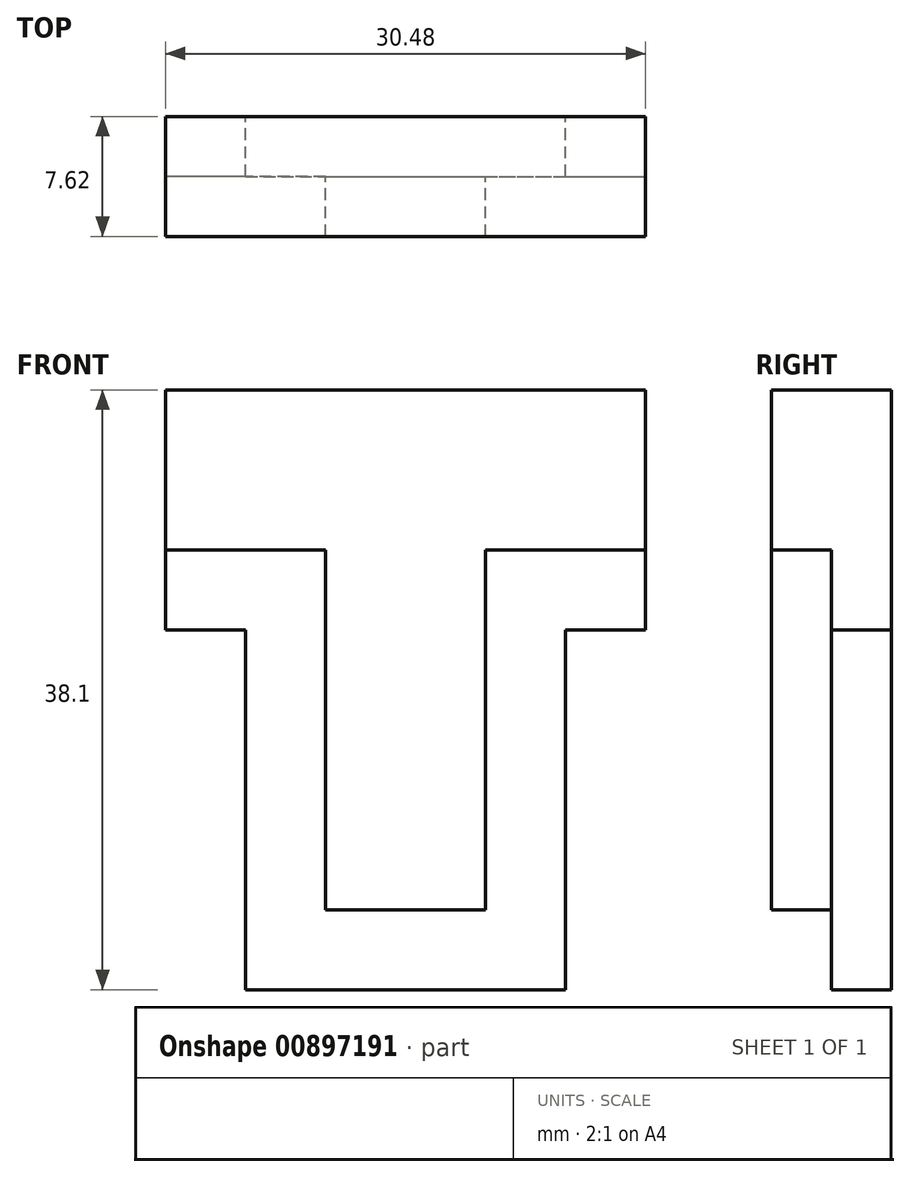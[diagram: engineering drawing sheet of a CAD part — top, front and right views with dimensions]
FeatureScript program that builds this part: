
annotation { "Feature Type Name" : "Feature", "Feature Type Description" : "" }
export const myFeature = defineFeature(function(context is Context, id is Id, definition is map)
    precondition{}
    {
        {
            var Q0;
            Q0=qCreatedBy(makeId("Front.planeOp"),FACE);
            var sketch = newSketch(context, id + "F0", { "sketchPlane" : qUnion([Q0])});
            skLineSegment(sketch, "E0.top", {"start": v(-25.4, -17.78) * mm, "end": v(-5.08, -17.78) * mm});
            skLineSegment(sketch, "E0.left", {"start": v(-25.4, 0) * mm, "end": v(-25.4, -17.78) * mm});
            skPoint(sketch, "E0.middle", {"position": v(0, 0) * mm});
            skLineSegment(sketch, "E1", {"start": v(-20.32, -17.78) * mm, "end": v(-20.32, 5.08) * mm});
            skLineSegment(sketch, "E2", {"start": v(-30.48, 15.24) * mm, "end": v(0, 15.24) * mm});
            skLineSegment(sketch, "E3", {"start": v(-10.16, -17.78) * mm, "end": v(-10.16, 5.08) * mm});
            skLineSegment(sketch, "E4", {"start": v(-10.16, 5.08) * mm, "end": v(0, 5.08) * mm});
            skLineSegment(sketch, "E5", {"start": v(-5.08, -17.78) * mm, "end": v(-5.08, 0) * mm});
            skLineSegment(sketch, "E6", {"start": v(-5.08, 0) * mm, "end": v(0, 0) * mm});
            skLineSegment(sketch, "E7", {"start": v(-25.4, -17.78) * mm, "end": v(-25.4, -22.86) * mm});
            skLineSegment(sketch, "E8", {"start": v(-25.4, -22.86) * mm, "end": v(-5.08, -22.86) * mm});
            skLineSegment(sketch, "E9", {"start": v(-5.08, -22.86) * mm, "end": v(-5.08, -17.78) * mm});
            skLineSegment(sketch, "E10", {"start": v(0, 0) * mm, "end": v(0, 5.08) * mm});
            skLineSegment(sketch, "E11", {"start": v(0, 5.08) * mm, "end": v(0, 15.24) * mm});
            skLineSegment(sketch, "E12", {"start": v(-25.4, 0) * mm, "end": v(-30.48, 0) * mm});
            skLineSegment(sketch, "E13", {"start": v(-30.48, 0) * mm, "end": v(-30.48, 15.24) * mm});
            skLineSegment(sketch, "E14", {"start": v(-20.32, 5.08) * mm, "end": v(-30.48, 5.08) * mm});
            skSolve(sketch);
        }
        {
            var Q0;
            {var subQ1=sQuery(id+"F0.wireOp",EDGE,"E1");Q0=makeQuery(id+"F0.imprint","IMPRINT",FACE,{"disambiguationData":[TD([[makeQuery(id+"F0.imprint","IMPRINT",EDGE,{"derivedFrom":subQ1}),-1.0]])]});}
            extrude(context, id + "F1", {"entities" : qUnion([Q0]), "depth" : 7.62 * mm, "offsetDistance" : 25.4 * mm});
        }
        {
            var Q0;
            Q0=makeQuery(id+"F0.imprint","IMPRINT",FACE,{"disambiguationData":[TD([[makeQuery(id+"F0.imprint","IMPRINT",EDGE,{"derivedFrom":sQuery(id+"F0.wireOp",EDGE,"E0.bottom")}),-1.0]])]});
            var Q1;
            {var subQ1=sQuery(id+"F0.wireOp",EDGE,"E3");Q1=makeQuery(id+"F0.imprint","IMPRINT",FACE,{"disambiguationData":[TD([[makeQuery(id+"F0.imprint","IMPRINT",EDGE,{"derivedFrom":subQ1}),-1.0]])]});}
            var Q2;
            {var subQ0=sQuery(id+"F0.wireOp",EDGE,"E7");Q2=makeQuery(id+"F0.imprint","IMPRINT",FACE,{"disambiguationData":[TD([[makeQuery(id+"F0.imprint","IMPRINT",EDGE,{"derivedFrom":subQ0}),1.0]])]});}
            var Q3;
            {var subQ3=sQuery(id+"F0.wireOp",EDGE,"IkdrzXF5-7qdE-oT8m-KYRU-39VJvmu7d8Oz");Q3=makeQuery(id+"F0.imprint","IMPRINT",FACE,{"disambiguationData":[TD([[makeQuery(id+"F0.imprint","IMPRINT",EDGE,{"derivedFrom":subQ3}),1.0]])]});}
            var Q4;
            {var subQ2=sQuery(id+"F0.wireOp",EDGE,"E0.left");Q4=makeQuery(id+"F0.imprint","IMPRINT",FACE,{"disambiguationData":[TD([[makeQuery(id+"F0.imprint","IMPRINT",EDGE,{"derivedFrom":subQ2}),1.0]])]});}
            extrude(context, id + "F2", {"entities" : qUnion([Q0, Q1, Q2, Q3, Q4]), "operationType" : NewBodyOperationType.ADD, "depth" : 3.8 * mm, "offsetDistance" : 25.4 * mm});
        }
    });
